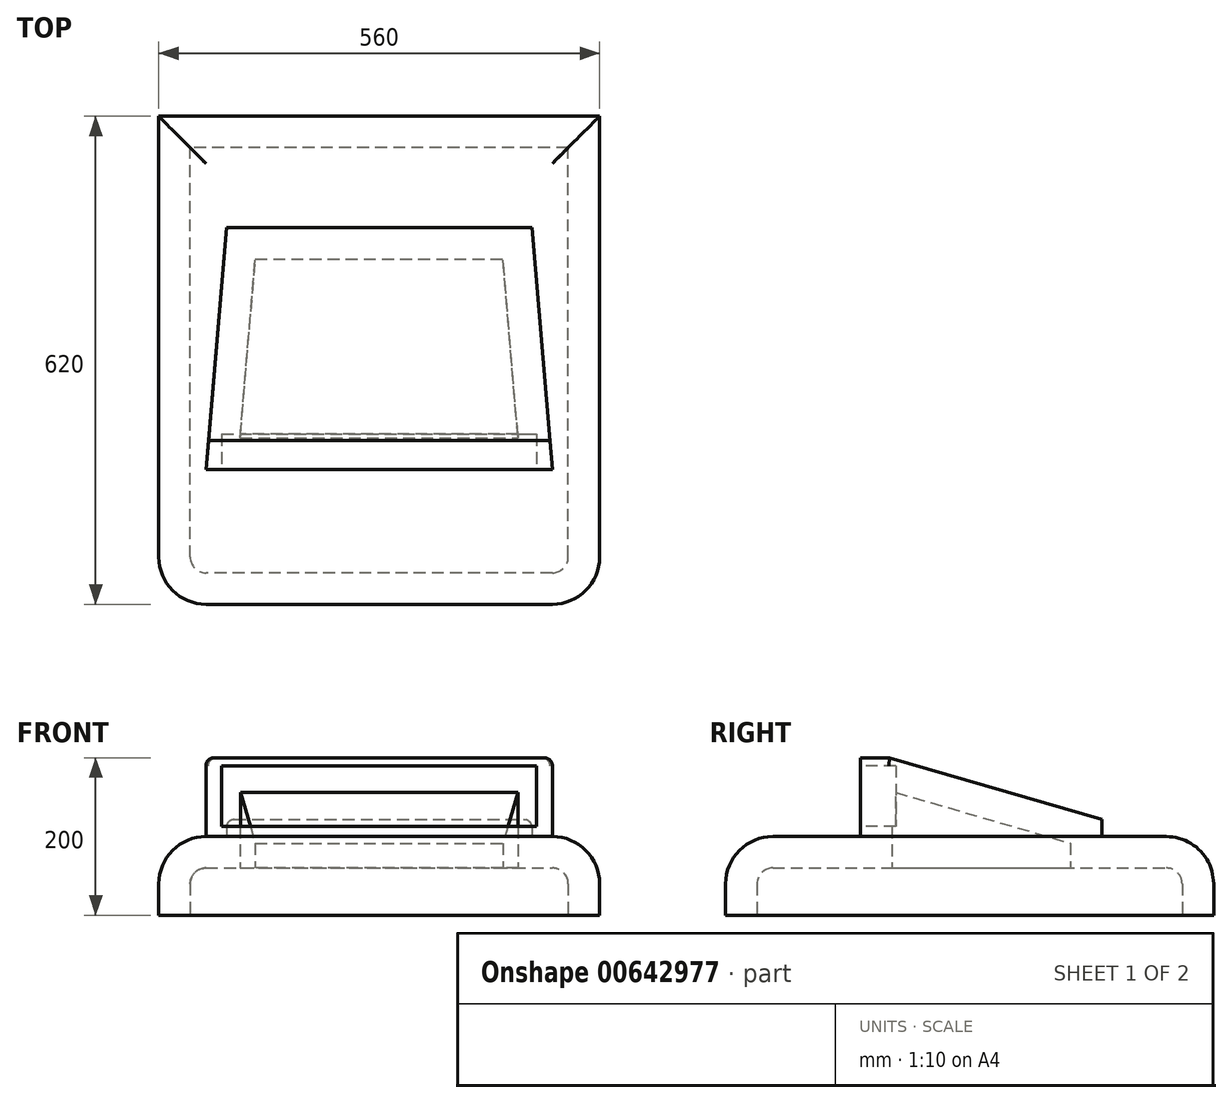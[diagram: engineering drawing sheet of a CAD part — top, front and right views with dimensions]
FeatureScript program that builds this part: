
annotation { "Feature Type Name" : "Feature", "Feature Type Description" : "" }
export const myFeature = defineFeature(function(context is Context, id is Id, definition is map)
    precondition{}
    {
        {
            var Q0;
            Q0=qCreatedBy(makeId("Top.planeOp"),FACE);
            var sketch = newSketch(context, id + "F0", { "sketchPlane" : qUnion([Q0])});
            skLineSegment(sketch, "E0.bottom", {"start": v(280, -310) * mm, "end": v(-280, -310) * mm});
            skLineSegment(sketch, "E0.top", {"start": v(280, 310) * mm, "end": v(-280, 310) * mm});
            skLineSegment(sketch, "E0.left", {"start": v(280, -310) * mm, "end": v(280, 310) * mm});
            skLineSegment(sketch, "E0.right", {"start": v(-280, -310) * mm, "end": v(-280, 310) * mm});
            skPoint(sketch, "E0.middle", {"position": v(0, 0) * mm});
            skSolve(sketch);
        }
        {
            var Q0;
            Q0=makeQuery(id+"F0.imprint","IMPRINT",FACE,{"disambiguationData":[TD([[makeQuery(id+"F0.imprint","IMPRINT",EDGE,{"derivedFrom":sQuery(id+"F0.wireOp",EDGE,"E0.bottom")}),-1.0]])]});
            extrude(context, id + "F1", {"entities" : qUnion([Q0]), "depth" : 100 * mm, "offsetDistance" : 25 * mm});
        }
        {
            var Q0;
            Q0=makeQuery(id+"F1.opExtrude","SWEPT_EDGE",EDGE,{"disambiguationData":[OSD([sQuery(id+"F0.wireOp",EDGE,"E0.bottom"),sQuery(id+"F0.wireOp",EDGE,"E0.left")])]});
            var Q1;
            Q1=makeQuery(id+"F1.opExtrude","SWEPT_EDGE",EDGE,{"disambiguationData":[OSD([sQuery(id+"F0.wireOp",EDGE,"E0.bottom"),sQuery(id+"F0.wireOp",EDGE,"E0.right")])]});
            fillet(context, id + "F2", {"entities" : qUnion([Q0, Q1]), "radius" : 60 * mm, "tangentPropagation" : true, "allowEdgeOverflow" : false});
        }
        {
            var Q0;
            Q0=makeQuery(id+"F1.opExtrude","CAP_FACE",FACE,{"disambiguationData":[OSD([sQuery(id+"F0.wireOp",EDGE,"E0.bottom"),sQuery(id+"F0.wireOp",EDGE,"E0.top"),sQuery(id+"F0.wireOp",EDGE,"E0.left"),sQuery(id+"F0.wireOp",EDGE,"E0.right")])],"isStart":false});
            fillet(context, id + "F3", {"entities" : qUnion([Q0]), "radius" : 60 * mm, "tangentPropagation" : true, "allowEdgeOverflow" : false});
        }
        {
            var Q0;
            Q0=makeQuery(id+"F1.opExtrude","CAP_FACE",FACE,{"disambiguationData":[OSD([sQuery(id+"F0.wireOp",EDGE,"E0.bottom"),sQuery(id+"F0.wireOp",EDGE,"E0.top"),sQuery(id+"F0.wireOp",EDGE,"E0.left"),sQuery(id+"F0.wireOp",EDGE,"E0.right")])],"isStart":false});
            var sketch = newSketch(context, id + "F4", { "sketchPlane" : qUnion([Q0])});
            skLineSegment(sketch, "E1", {"start": v(-220, -138.75) * mm, "end": v(0, -138.75) * mm});
            skLineSegment(sketch, "E2", {"start": v(-220, -138.75) * mm, "end": v(-194.13, 168.35) * mm});
            skLineSegment(sketch, "E3", {"start": v(-194.13, 168.35) * mm, "end": v(0, 168.35) * mm});
            skLineSegment(sketch, "E4", {"start": v(0, 0) * mm, "end": v(0, 373.93) * mm});
            skLineSegment(sketch, "E5.MirrorCS", {"start": v(194.13, 168.35) * mm, "end": v(0, 168.35) * mm});
            skLineSegment(sketch, "E6.MirrorCS", {"start": v(220, -138.75) * mm, "end": v(194.13, 168.35) * mm});
            skLineSegment(sketch, "E7.MirrorCS", {"start": v(220, -138.75) * mm, "end": v(0, -138.75) * mm});
            skSolve(sketch);
        }
        {
            var Q0;
            Q0=makeQuery(id+"F4.imprint","IMPRINT",FACE,{"disambiguationData":[TD([[makeQuery(id+"F4.imprint","IMPRINT",EDGE,{"derivedFrom":sQuery(id+"F4.wireOp",EDGE,"E1")}),1.0]])]});
            extrude(context, id + "F5", {"entities" : qUnion([Q0]), "operationType" : NewBodyOperationType.ADD, "depth" : 100 * mm, "offsetDistance" : 25 * mm});
        }
        {
            var Q0;
            Q0=makeQuery(id+"F1.opExtrude","SWEPT_FACE",FACE,{"disambiguationData":[OSD([sQuery(id+"F0.wireOp",EDGE,"E0.left")])]});
            var sketch = newSketch(context, id + "F6", { "sketchPlane" : qUnion([Q0])});
            skLineSegment(sketch, "E8", {"start": v(-166.55, 218.71) * mm, "end": v(222.8, 105.7) * mm});
            skLineSegment(sketch, "E9", {"start": v(222.8, 105.7) * mm, "end": v(261.03, 237.4) * mm});
            skLineSegment(sketch, "E10", {"start": v(261.03, 237.4) * mm, "end": v(-149, 213.62) * mm});
            skSolve(sketch);
        }
        {
            var Q0;
            Q0 = qSketchRegion(id + "F6", true);
            extrude(context, id + "F7", {"entities" : qUnion([Q0]), "operationType" : NewBodyOperationType.REMOVE, "endBound" : BoundingType.THROUGH_ALL, "oppositeDirection" : true, "depth" : 25 * mm, "offsetDistance" : 25 * mm});
        }
        {
            var Q0;
            Q0=makeQuery(id+"F5.opExtrude","CAP_EDGE",EDGE,{"disambiguationData":[OSD([sQuery(id+"F4.wireOp",EDGE,"E6.MirrorCS")])],"isStart":false});
            var Q1;
            Q1=makeQuery(id+"F7.boolean.opBoolean","INTERSECT",EDGE,{"derivedFrom":[makeQuery(id+"F5.opExtrude","SWEPT_FACE",FACE,{"disambiguationData":[OSD([sQuery(id+"F4.wireOp",EDGE,"E6.MirrorCS")])]}),makeQuery(id+"F7.opExtrude","SWEPT_FACE",FACE,{"disambiguationData":[OSD([sQuery(id+"F6.wireOp",EDGE,"E8")])]})]});
            var Q2;
            Q2=makeQuery(id+"F5.opExtrude","CAP_EDGE",EDGE,{"disambiguationData":[OSD([sQuery(id+"F4.wireOp",EDGE,"E2")])],"isStart":false});
            var Q3;
            Q3=makeQuery(id+"F7.boolean.opBoolean","INTERSECT",EDGE,{"derivedFrom":[makeQuery(id+"F5.opExtrude","SWEPT_FACE",FACE,{"disambiguationData":[OSD([sQuery(id+"F4.wireOp",EDGE,"E2")])]}),makeQuery(id+"F7.opExtrude","SWEPT_FACE",FACE,{"disambiguationData":[OSD([sQuery(id+"F6.wireOp",EDGE,"E8")])]})]});
            fillet(context, id + "F8", {"entities" : qUnion([Q0, Q1, Q2, Q3]), "radius" : 10 * mm, "tangentPropagation" : true, "allowEdgeOverflow" : false});
        }
        {
            var Q0;
            Q0=makeQuery(id+"F5.opExtrude","SWEPT_FACE",FACE,{"disambiguationData":[OSD([sQuery(id+"F4.wireOp",EDGE,"E1"),sQuery(id+"F4.wireOp",EDGE,"E7.MirrorCS")])]});
            var sketch = newSketch(context, id + "F9", { "sketchPlane" : qUnion([Q0])});
            skLineSegment(sketch, "E11.bottom", {"start": v(-199.93, 190) * mm, "end": v(200, 190) * mm});
            skLineSegment(sketch, "E11.top", {"start": v(-199.93, 112.84) * mm, "end": v(200, 112.84) * mm});
            skLineSegment(sketch, "E11.left", {"start": v(-199.93, 190) * mm, "end": v(-199.93, 112.84) * mm});
            skLineSegment(sketch, "E11.right", {"start": v(200, 190) * mm, "end": v(200, 112.84) * mm});
            skSolve(sketch);
        }
        {
            var Q0;
            Q0=makeQuery(id+"F1.opExtrude","CAP_FACE",FACE,{"disambiguationData":[OSD([sQuery(id+"F0.wireOp",EDGE,"E0.bottom"),sQuery(id+"F0.wireOp",EDGE,"E0.top"),sQuery(id+"F0.wireOp",EDGE,"E0.left"),sQuery(id+"F0.wireOp",EDGE,"E0.right")])],"isStart":true});
            shell(context, id + "F10", {"entities" : qUnion([Q0]), "thickness" : 40 * mm});
        }
        {
            var Q0;
            Q0=makeQuery(id+"F9.imprint","IMPRINT",FACE,{"disambiguationData":[TD([[makeQuery(id+"F9.imprint","IMPRINT",EDGE,{"derivedFrom":sQuery(id+"F9.wireOp",EDGE,"E11.bottom")}),-1.0]])]});
            extrude(context, id + "F11", {"entities" : qUnion([Q0]), "operationType" : NewBodyOperationType.REMOVE, "oppositeDirection" : true, "depth" : 45 * mm, "offsetDistance" : 25 * mm});
        }
    });
